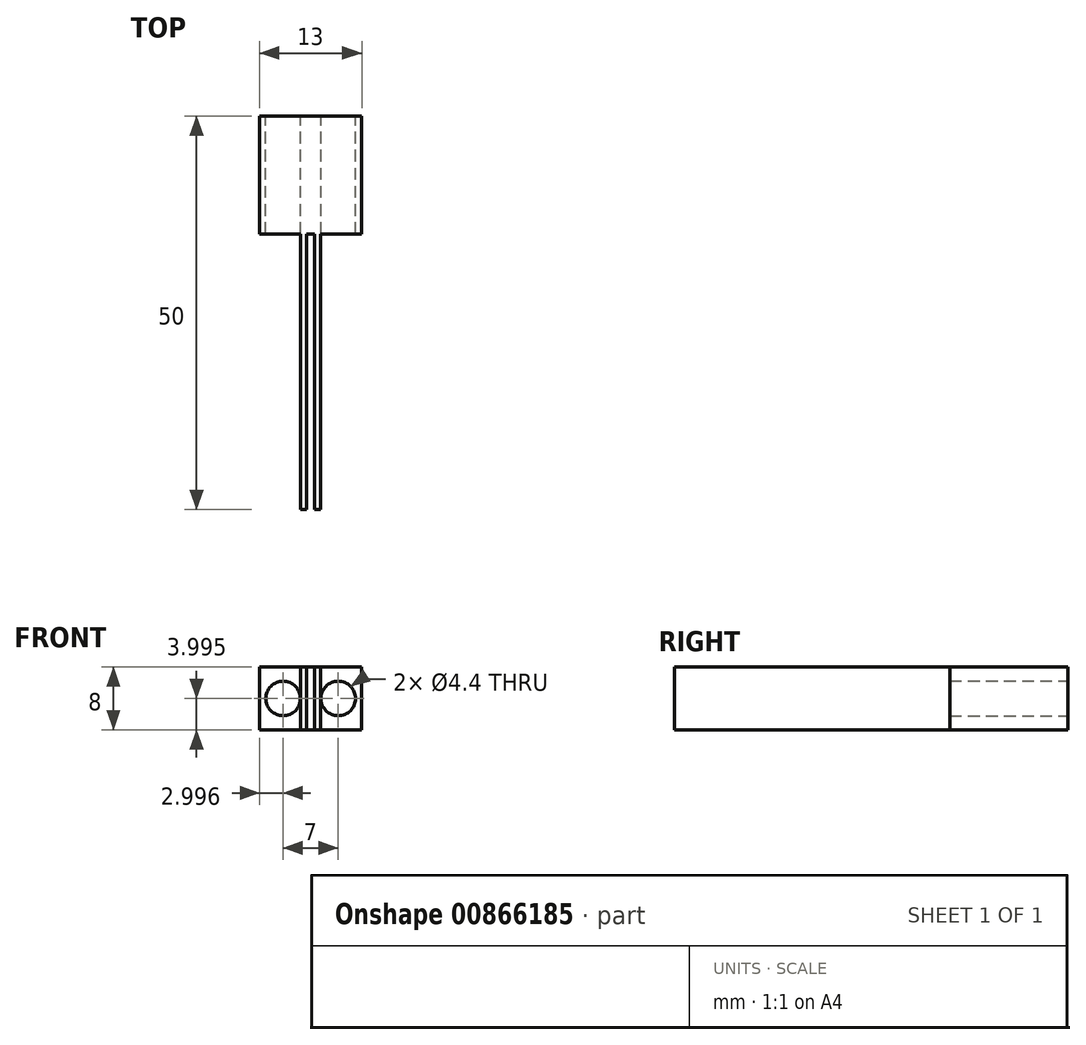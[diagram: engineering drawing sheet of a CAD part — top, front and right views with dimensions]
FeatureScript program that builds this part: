
annotation { "Feature Type Name" : "Feature", "Feature Type Description" : "" }
export const myFeature = defineFeature(function(context is Context, id is Id, definition is map)
    precondition{}
    {
        {
            var Q0;
            Q0=qCreatedBy(makeId("Front.planeOp"),FACE);
            var sketch = newSketch(context, id + "F0", { "sketchPlane" : qUnion([Q0])});
            skLineSegment(sketch, "E0.bottom", {"start": v(-67.37, 27.37) * mm, "end": v(-54.37, 27.37) * mm});
            skLineSegment(sketch, "E0.top", {"start": v(-67.37, 19.37) * mm, "end": v(-61.37, 19.37) * mm});
            skLineSegment(sketch, "E0.left", {"start": v(-67.37, 27.37) * mm, "end": v(-67.37, 19.37) * mm});
            skLineSegment(sketch, "E0.right", {"start": v(-54.37, 27.37) * mm, "end": v(-54.37, 19.37) * mm});
            skLineSegment(sketch, "E1", {"start": v(-61.37, 27.37) * mm, "end": v(-61.37, 19.37) * mm});
            skLineSegment(sketch, "E2", {"start": v(-60.37, 19.37) * mm, "end": v(-60.37, 27.37) * mm});
            skPoint(sketch, "E3", {"position": v(-61.37, 19.37) * mm});
            skPoint(sketch, "E4", {"position": v(-60.37, 19.37) * mm});
            skLineSegment(sketch, "E5.trimOffspring", {"start": v(-60.37, 19.37) * mm, "end": v(-54.37, 19.37) * mm});
            skLineSegment(sketch, "E6", {"start": v(-61.37, 19.37) * mm, "end": v(-60.37, 19.37) * mm});
            skCircle(sketch, "E7", {"center": v(-64.37, 23.37) * mm, "radius": 2.2 * mm});
            skPoint(sketch, "E7.centerSnap0", {"position": v(-67.37, 23.37) * mm});
            skPoint(sketch, "E7.centerSnap1", {"position": v(-64.37, 19.37) * mm});
            skCircle(sketch, "E8", {"center": v(-57.37, 23.37) * mm, "radius": 2.2 * mm});
            skPoint(sketch, "E8.centerSnap0", {"position": v(-54.37, 23.37) * mm});
            skPoint(sketch, "E8.centerSnap1", {"position": v(-57.37, 19.37) * mm});
            skLineSegment(sketch, "E9", {"start": v(-62.17, 19.37) * mm, "end": v(-62.17, 27.37) * mm});
            skLineSegment(sketch, "E10", {"start": v(-59.57, 19.37) * mm, "end": v(-59.57, 27.37) * mm});
            skSolve(sketch);
        }
        {
            var Q0;
            Q0 = qSketchRegion(id + "F0", true);
            extrude(context, id + "F1", {"entities" : qUnion([Q0]), "depth" : 15 * mm, "offsetDistance" : 25 * mm});
        }
        {
            var Q0;
            Q0=makeQuery(id+"F1.opExtrude","CAP_FACE",FACE,{"disambiguationData":[OSD([sQuery(id+"F0.wireOp",EDGE,"E0.bottom"),sQuery(id+"F0.wireOp",EDGE,"E0.top"),sQuery(id+"F0.wireOp",EDGE,"E0.left"),sQuery(id+"F0.wireOp",EDGE,"E0.right"),sQuery(id+"F0.wireOp",EDGE,"E5.trimOffspring"),sQuery(id+"F0.wireOp",EDGE,"E6"),sQuery(id+"F0.wireOp",EDGE,"E7"),sQuery(id+"F0.wireOp",EDGE,"E8")])],"isStart":false});
            var sketch = newSketch(context, id + "F2", { "sketchPlane" : qUnion([Q0])});
            skLineSegment(sketch, "E11.0", {"start": v(-62.16, 27.37) * mm, "end": v(-59.6, 27.37) * mm});
            skLineSegment(sketch, "E12.0", {"start": v(-62.16, 19.37) * mm, "end": v(-61.37, 19.37) * mm});
            skLineSegment(sketch, "E13.0", {"start": v(-60.37, 19.37) * mm, "end": v(-59.6, 19.37) * mm});
            skPoint(sketch, "E14.0", {"position": v(-60.87, 19.37) * mm});
            skLineSegment(sketch, "E15.0", {"start": v(-61.37, 19.37) * mm, "end": v(-60.37, 19.37) * mm});
            skLineSegment(sketch, "E16", {"start": v(-62.16, 27.37) * mm, "end": v(-62.16, 19.37) * mm});
            skLineSegment(sketch, "E17", {"start": v(-61.37, 19.37) * mm, "end": v(-61.37, 27.37) * mm});
            skLineSegment(sketch, "E18", {"start": v(-59.6, 27.37) * mm, "end": v(-59.6, 19.37) * mm});
            skLineSegment(sketch, "E19", {"start": v(-60.37, 19.37) * mm, "end": v(-60.37, 27.37) * mm});
            skLineSegment(sketch, "E20", {"start": v(-59.6, 27.37) * mm, "end": v(-62.16, 27.37) * mm});
            skLineSegment(sketch, "E21", {"start": v(-62.16, 19.37) * mm, "end": v(-59.6, 19.37) * mm});
            skPoint(sketch, "E22.orphan", {"position": v(-67.37, 27.37) * mm});
            skPoint(sketch, "E23.orphan", {"position": v(-67.37, 19.37) * mm});
            skPoint(sketch, "E24.orphan", {"position": v(-54.37, 19.37) * mm});
            skPoint(sketch, "E25.orphan", {"position": v(-54.37, 27.37) * mm});
            skSolve(sketch);
        }
        {
            var Q0;
            {var subQ0=sQuery(id+"F2.wireOp",EDGE,"E16");Q0=makeQuery(id+"F2.imprint","IMPRINT",FACE,{"disambiguationData":[TD([[makeQuery(id+"F2.imprint","IMPRINT",EDGE,{"derivedFrom":subQ0}),1.0]])]});}
            var Q1;
            {var subQ0=sQuery(id+"F2.wireOp",EDGE,"E18");Q1=makeQuery(id+"F2.imprint","IMPRINT",FACE,{"disambiguationData":[TD([[makeQuery(id+"F2.imprint","IMPRINT",EDGE,{"derivedFrom":subQ0}),-1.0]])]});}
            extrude(context, id + "F3", {"entities" : qUnion([Q0, Q1]), "operationType" : NewBodyOperationType.ADD, "depth" : 35 * mm, "offsetDistance" : 25 * mm});
        }
    });
